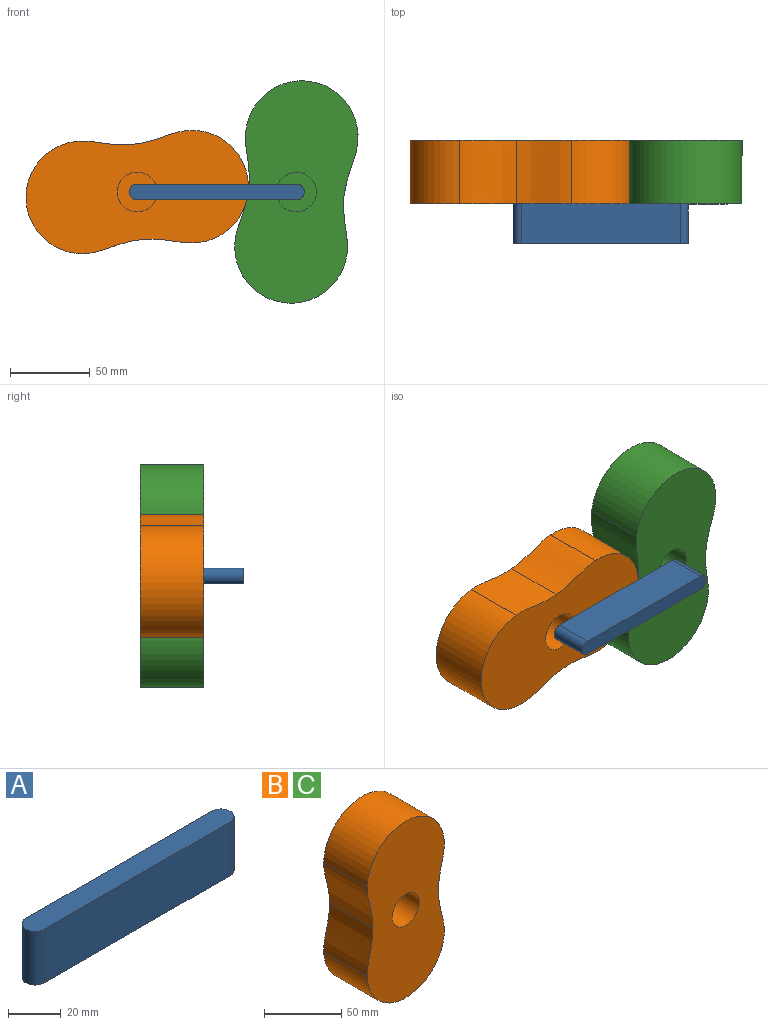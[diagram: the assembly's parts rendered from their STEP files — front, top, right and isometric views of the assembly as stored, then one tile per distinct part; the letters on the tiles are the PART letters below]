
ASSEMBLY  parts=3 mates=2
PART A: 6 faces, bbox 110x10x25 mm
  f0: cylinder r=5mm len=25mm, axis (0,0,-1), area 392.7mm2, adj f1,f3,f4,f5
  f1: plane 100x25mm, normal (0,-1,0), area 2500mm2, adj f0,f2,f4,f5
  f2: cylinder r=5mm len=25mm, axis (0,0,-1), area 392.7mm2, adj f1,f3,f4,f5
  f3: plane 100x25mm, normal (0,1,0), area 2500mm2, adj f0,f2,f4,f5
  f4: plane 110x10mm, normal (0,0,1), area 1078.5mm2, adj f0,f1,f2,f3
  f5: plane 110x10mm, normal (0,0,-1), area 1078.5mm2, adj f0,f1,f2,f3
PART B: 17 faces, bbox 70.7x39.8x140 mm
  f0: extruded ~39.8x35.33mm, area 1426.5mm2, adj f1,f9,f10,f11
  f1: extruded ~39.8x35.33mm, area 1426.5mm2, adj f0,f2,f10,f11
  f2: plane 39.8x0.03mm, normal (-1,0,-0.02), area 1.1mm2, adj f1,f3,f10,f11
  f3: cylinder r=35.36mm len=70.71mm, axis (0,1,0), area 4364.4mm2, adj f2,f4,f10,f11
  f4: plane 39.8x0.03mm, normal (1,0,-0.02), area 1.1mm2, adj f3,f5,f10,f11
  f5: extruded ~39.8x35.33mm, area 1426.5mm2, adj f4,f6,f10,f11
  f6: extruded ~39.8x35.33mm, area 1426.5mm2, adj f5,f7,f10,f11
  f7: plane 39.8x0.03mm, normal (1,0,0.02), area 1.1mm2, adj f6,f8,f10,f11
  f8: cylinder r=35.36mm len=70.71mm, axis (0,1,0), area 4364.4mm2, adj f7,f9,f10,f11
  f9: plane 39.8x0.03mm, normal (-1,0,0.02), area 1.1mm2, adj f0,f8,f10,f11
  f10: plane 140x70.73mm, normal (0,-1,0), area 7942.3mm2, adj f0,f1,f2,f3,f4,f5,f6,f7
  f11: plane 140x70.73mm, normal (0,1,0), area 8119mm2, adj f0,f1,f2,f3,f4,f5,f6,f7
  f12: cylinder r=12.5mm len=25mm, axis (0,-1,0), area 1955.6mm2, adj f10,f13
  f13: plane 25x25mm, normal (0,-1,0), area 412.3mm2, adj f12,f16
  f14: cylinder r=10mm len=20mm, axis (0,1,0), area 628.3mm2, adj f11,f15
  f15: plane 20x20mm, normal (0,1,0), area 235.6mm2, adj f14,f16
  f16: cylinder r=5mm len=10mm, axis (0,-1,0), area 153.9mm2, adj f13,f15
PART C: same geometry as B
PLACE A rot(axis=(-1,0,0),90deg) t=(-56.96,28.47,88.34)mm fixed
PLACE B rot(axis=(0,-1,0),95.5deg) t=(-74.45,73.37,67.87)mm
PLACE C rot(axis=(0,1,0),5.5deg) t=(25.55,73.37,67.87)mm
MATE revolute A.f2 <-> C.f16  axis (0,-1,0) through (25.55,53.47,67.87)mm
MATE revolute B.f12 <-> A.f0  axis (0,-1,0) through (-74.45,53.47,67.87)mm
